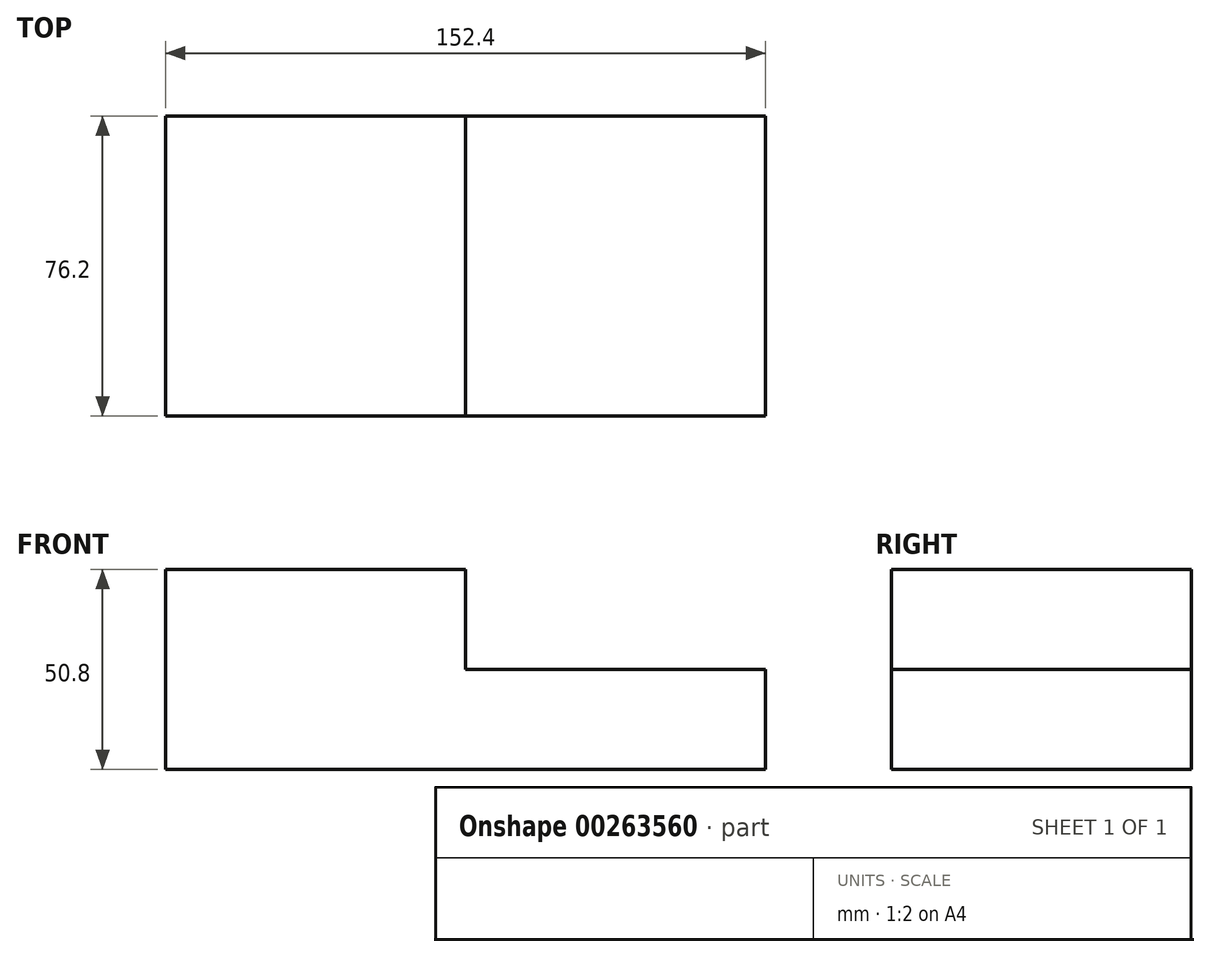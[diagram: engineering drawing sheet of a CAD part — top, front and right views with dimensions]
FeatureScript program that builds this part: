
annotation { "Feature Type Name" : "Feature", "Feature Type Description" : "" }
export const myFeature = defineFeature(function(context is Context, id is Id, definition is map)
    precondition{}
    {
        {
            var Q0;
            Q0=qCreatedBy(makeId("Front.planeOp"),FACE);
            var sketch = newSketch(context, id + "F0", { "sketchPlane" : qUnion([Q0])});
            skLineSegment(sketch, "E0", {"start": v(-76.2, -54.22) * mm, "end": v(76.2, -54.22) * mm});
            skLineSegment(sketch, "E1", {"start": v(76.2, -54.22) * mm, "end": v(76.2, -28.82) * mm});
            skLineSegment(sketch, "E2", {"start": v(76.2, -28.82) * mm, "end": v(0, -28.82) * mm});
            skLineSegment(sketch, "E3", {"start": v(0, -28.82) * mm, "end": v(0, -3.42) * mm});
            skLineSegment(sketch, "E4", {"start": v(0, -3.42) * mm, "end": v(-76.2, -3.42) * mm});
            skLineSegment(sketch, "E5", {"start": v(-76.2, -3.42) * mm, "end": v(-76.2, -54.22) * mm});
            skSolve(sketch);
        }
        {
            var Q0;
            Q0=makeQuery(id+"F0.imprint","IMPRINT",FACE,{"disambiguationData":[TD([[makeQuery(id+"F0.imprint","IMPRINT",EDGE,{"derivedFrom":sQuery(id+"F0.wireOp",EDGE,"E0")}),1.0]])]});
            extrude(context, id + "F1", {"entities" : qUnion([Q0]), "depth" : 76.2 * mm});
        }
    });
